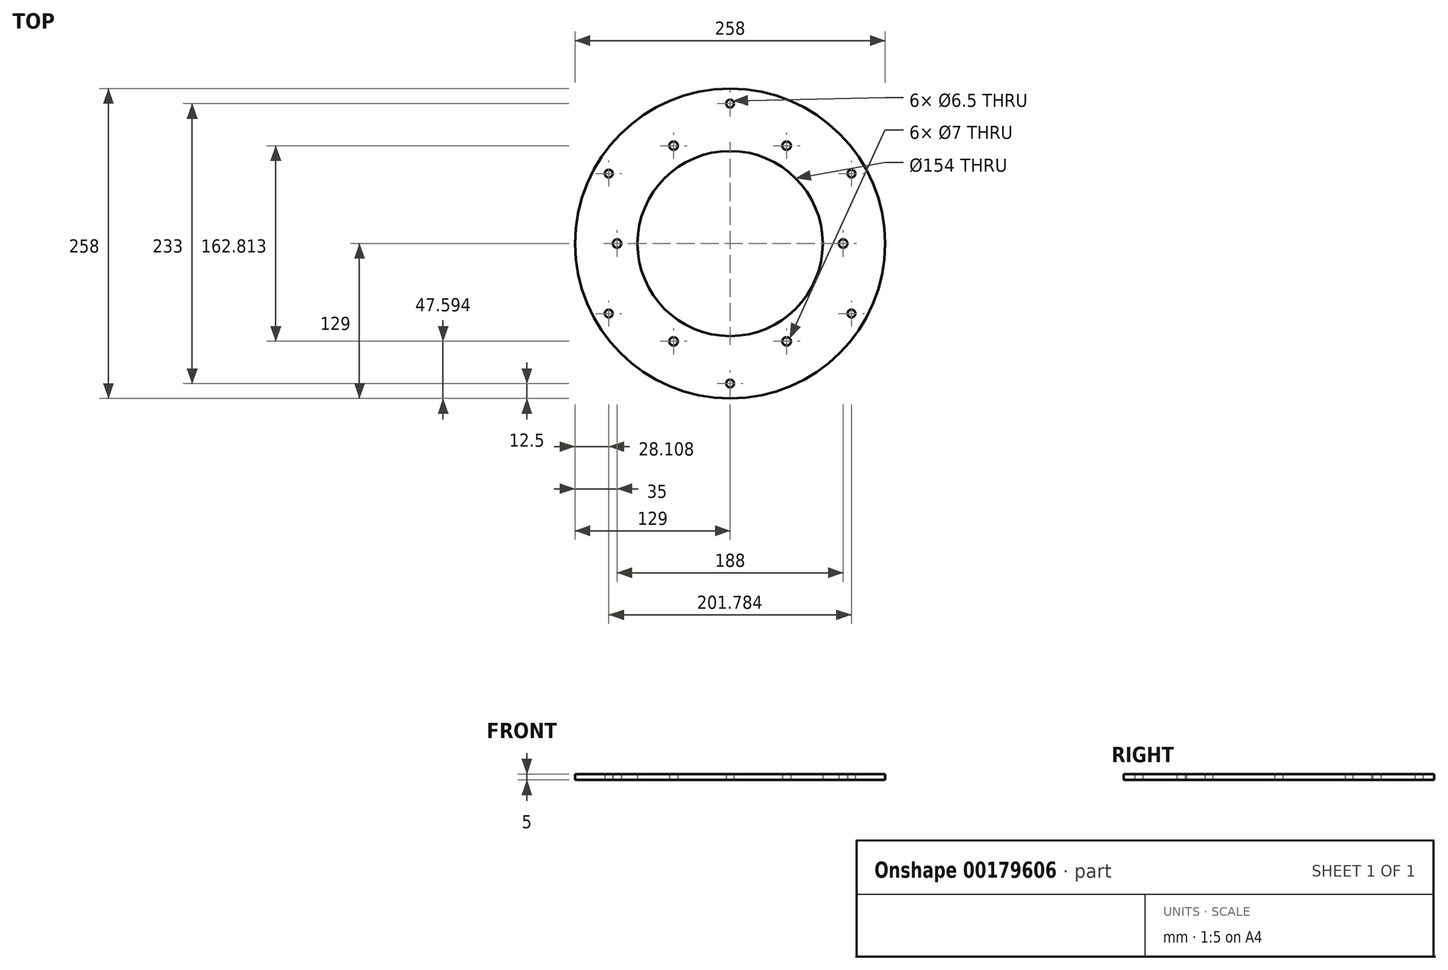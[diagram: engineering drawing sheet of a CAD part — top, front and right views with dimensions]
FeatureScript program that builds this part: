
annotation { "Feature Type Name" : "Feature", "Feature Type Description" : "" }
export const myFeature = defineFeature(function(context is Context, id is Id, definition is map)
    precondition{}
    {
        {
            var Q0;
            Q0=qCreatedBy(makeId("Top.planeOp"),FACE);
            var sketch = newSketch(context, id + "F0", { "sketchPlane" : qUnion([Q0])});
            skCircle(sketch, "E0", {"center": v(0, 0) * mm, "radius": 104 * mm, "construction": true});
            skCircle(sketch, "E1", {"center": v(0, 0) * mm, "radius": 129 * mm});
            skCircle(sketch, "E2", {"center": v(0, 116.5) * mm, "radius": 3.25 * mm});
            skLineSegment(sketch, "E3", {"start": v(0, 104) * mm, "end": v(0, 129) * mm, "construction": true});
            skCircle(sketch, "E4.cCircle", {"center": v(0, 0) * mm, "radius": 116.5 * mm, "construction": true});
            skLineSegment(sketch, "E4.0", {"start": v(0, 116.5) * mm, "end": v(100.9, 58.25) * mm, "construction": true});
            skLineSegment(sketch, "E4.1", {"start": v(100.9, 58.25) * mm, "end": v(100.9, -58.25) * mm, "construction": true});
            skLineSegment(sketch, "E4.2", {"start": v(100.9, -58.25) * mm, "end": v(0, -116.5) * mm, "construction": true});
            skLineSegment(sketch, "E4.3", {"start": v(0, -116.5) * mm, "end": v(-100.9, -58.25) * mm, "construction": true});
            skLineSegment(sketch, "E4.4", {"start": v(-100.9, -58.25) * mm, "end": v(-100.9, 58.25) * mm, "construction": true});
            skLineSegment(sketch, "E4.5", {"start": v(-100.9, 58.25) * mm, "end": v(0, 116.5) * mm, "construction": true});
            skCircle(sketch, "E5", {"center": v(100.9, 58.25) * mm, "radius": 3.25 * mm});
            skCircle(sketch, "E6", {"center": v(100.9, -58.25) * mm, "radius": 3.25 * mm});
            skCircle(sketch, "E7", {"center": v(0, -116.5) * mm, "radius": 3.25 * mm});
            skCircle(sketch, "E8", {"center": v(-100.9, -58.25) * mm, "radius": 3.25 * mm});
            skCircle(sketch, "E9", {"center": v(-100.9, 58.25) * mm, "radius": 3.25 * mm});
            skCircle(sketch, "E10", {"center": v(0, 0) * mm, "radius": 77 * mm});
            skCircle(sketch, "E11", {"center": v(0, 0) * mm, "radius": 94 * mm, "construction": true});
            skPoint(sketch, "E12", {"position": v(-50.45, 87.38) * mm});
            skLineSegment(sketch, "E13", {"start": v(0, 0) * mm, "end": v(-50.45, 87.37) * mm, "construction": true});
            skLineSegment(sketch, "E14.0", {"start": v(-47, 81.4) * mm, "end": v(47, 81.4) * mm, "construction": true});
            skLineSegment(sketch, "E14.1", {"start": v(47, 81.4) * mm, "end": v(94, 0) * mm, "construction": true});
            skLineSegment(sketch, "E14.2", {"start": v(94, 0) * mm, "end": v(47, -81.4) * mm, "construction": true});
            skLineSegment(sketch, "E14.3", {"start": v(47, -81.4) * mm, "end": v(-47, -81.4) * mm, "construction": true});
            skLineSegment(sketch, "E14.4", {"start": v(-47, -81.4) * mm, "end": v(-94, 0) * mm, "construction": true});
            skLineSegment(sketch, "E14.5", {"start": v(-94, 0) * mm, "end": v(-47, 81.4) * mm, "construction": true});
            skCircle(sketch, "E15", {"center": v(-47, 81.4) * mm, "radius": 3.5 * mm});
            skCircle(sketch, "E16", {"center": v(47, 81.4) * mm, "radius": 3.5 * mm});
            skCircle(sketch, "E17", {"center": v(94, 0) * mm, "radius": 3.5 * mm});
            skCircle(sketch, "E18", {"center": v(47, -81.4) * mm, "radius": 3.5 * mm});
            skCircle(sketch, "E19", {"center": v(-47, -81.4) * mm, "radius": 3.5 * mm});
            skCircle(sketch, "E20", {"center": v(-94, 0) * mm, "radius": 3.5 * mm});
            skSolve(sketch);
        }
        {
            var Q0;
            Q0=makeQuery(id+"F0.imprint","IMPRINT",FACE,{"disambiguationData":[TD([[makeQuery(id+"F0.imprint","IMPRINT",EDGE,{"derivedFrom":sQuery(id+"F0.wireOp",EDGE,"E1")}),1.0]])]});
            extrude(context, id + "F1", {"entities" : qUnion([Q0]), "depth" : 5 * mm});
        }
    });
